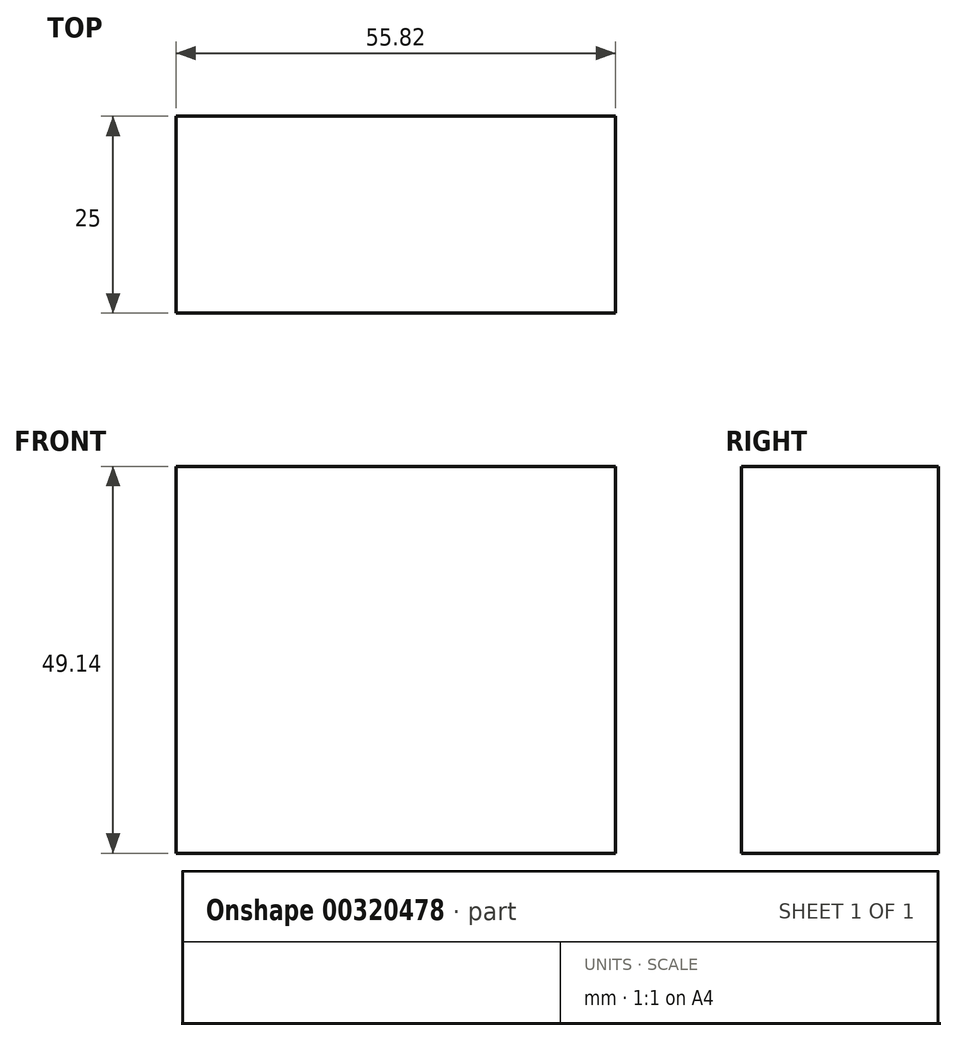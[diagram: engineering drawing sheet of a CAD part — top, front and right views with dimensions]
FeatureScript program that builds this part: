
annotation { "Feature Type Name" : "Feature", "Feature Type Description" : "" }
export const myFeature = defineFeature(function(context is Context, id is Id, definition is map)
    precondition{}
    {
        {
            var Q0;
            Q0=qCreatedBy(makeId("Front.planeOp"),FACE);
            var sketch = newSketch(context, id + "F0", { "sketchPlane" : qUnion([Q0])});
            skLineSegment(sketch, "E0.bottom", {"start": v(-91.2, 0) * mm, "end": v(-35.38, 0) * mm});
            skLineSegment(sketch, "E0.top", {"start": v(-91.2, 49.14) * mm, "end": v(-35.38, 49.14) * mm});
            skLineSegment(sketch, "E0.left", {"start": v(-91.2, 0) * mm, "end": v(-91.2, 49.14) * mm});
            skLineSegment(sketch, "E0.right", {"start": v(-35.38, 0) * mm, "end": v(-35.38, 49.14) * mm});
            skPoint(sketch, "E0.middle", {"position": v(-63.29, 24.57) * mm});
            skSolve(sketch);
        }
        {
            var Q0;
            Q0=makeQuery(id+"F0.imprint","IMPRINT",FACE,{"disambiguationData":[TD([[makeQuery(id+"F0.imprint","IMPRINT",EDGE,{"derivedFrom":sQuery(id+"F0.wireOp",EDGE,"E0.bottom")}),1.0]])]});
            extrude(context, id + "F1", {"entities" : qUnion([Q0]), "depth" : 25 * mm});
        }
    });
